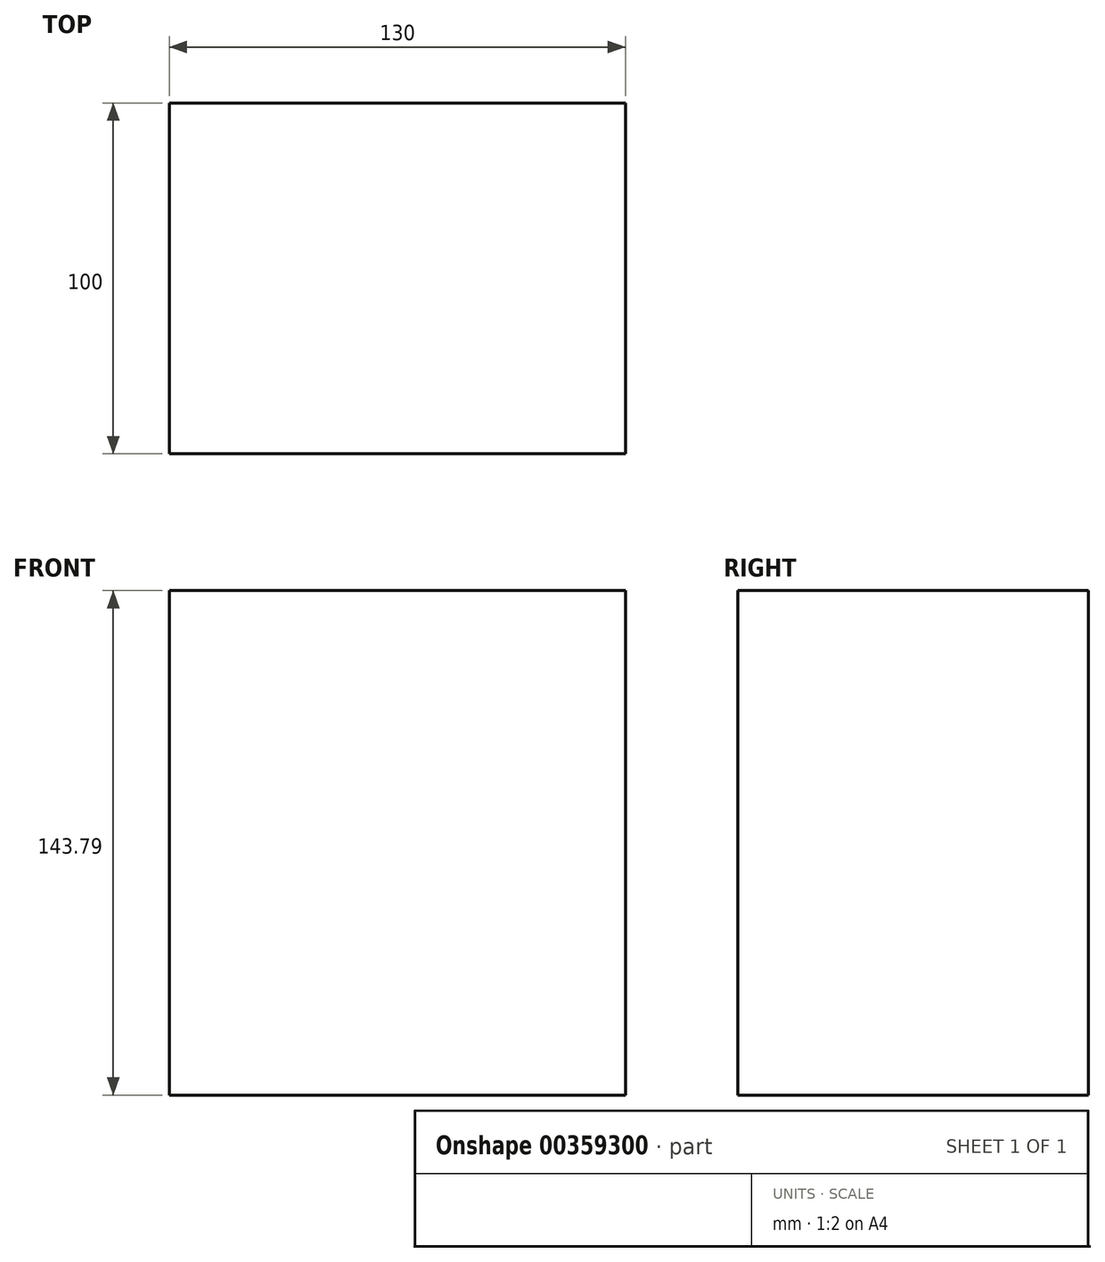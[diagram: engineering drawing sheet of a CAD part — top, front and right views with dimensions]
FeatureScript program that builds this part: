
annotation { "Feature Type Name" : "Feature", "Feature Type Description" : "" }
export const myFeature = defineFeature(function(context is Context, id is Id, definition is map)
    precondition{}
    {
        {
            var Q0;
            Q0=qCreatedBy(makeId("Top.planeOp"),FACE);
            var sketch = newSketch(context, id + "F0", { "sketchPlane" : qUnion([Q0])});
            skLineSegment(sketch, "E0.bottom", {"start": v(-65, 50) * mm, "end": v(65, 50) * mm});
            skLineSegment(sketch, "E0.top", {"start": v(-65, -50) * mm, "end": v(65, -50) * mm});
            skLineSegment(sketch, "E0.left", {"start": v(-65, 50) * mm, "end": v(-65, -50) * mm});
            skLineSegment(sketch, "E0.right", {"start": v(65, 50) * mm, "end": v(65, -50) * mm});
            skPoint(sketch, "E0.middle", {"position": v(0, 0) * mm});
            skSolve(sketch);
        }
        {
            var Q0;
            Q0=makeQuery(id+"F0.imprint","IMPRINT",FACE,{"disambiguationData":[TD([[makeQuery(id+"F0.imprint","IMPRINT",EDGE,{"derivedFrom":sQuery(id+"F0.wireOp",EDGE,"E0.bottom")}),-1.0]])]});
            extrude(context, id + "F1", {"entities" : qUnion([Q0]), "oppositeDirection" : true, "depth" : 180 * mm});
        }
        {
            var Q0;
            Q0=makeQuery(id+"F1.opExtrude","CAP_EDGE",EDGE,{"disambiguationData":[OSD([sQuery(id+"F0.wireOp",EDGE,"E0.right")])],"isStart":false});
            var Q1;
            Q1=makeQuery(id+"F1.opExtrude","CAP_EDGE",EDGE,{"disambiguationData":[OSD([sQuery(id+"F0.wireOp",EDGE,"E0.left")])],"isStart":false});
            fillet(context, id + "F2", {"entities" : qUnion([Q0, Q1]), "radius" : 36.2 * mm, "tangentPropagation" : true, "allowEdgeOverflow" : false});
        }
        {
            var Q0;
            Q0=makeQuery(id+"F1.opExtrude","SWEPT_FACE",FACE,{"disambiguationData":[OSD([sQuery(id+"F0.wireOp",EDGE,"E0.top")])]});
            var sketch = newSketch(context, id + "F3", { "sketchPlane" : qUnion([Q0])});
            skLineSegment(sketch, "E1", {"start": v(65, -143.79) * mm, "end": v(-65, -143.79) * mm});
            skSolve(sketch);
        }
        {
            var Q0;
            Q0 = qSketchRegion(id + "F3", true);
            var Q1;
            Q1=makeQuery(id+"F3.imprint","IMPRINT",FACE,{"disambiguationData":[TD([[makeQuery(id+"F3.imprint","IMPRINT",EDGE,{"derivedFrom":sQuery(id+"F3.wireOp",EDGE,"E1")}),1.0]])]});
            extrude(context, id + "F4", {"entities" : qUnion([Q0, Q1]), "operationType" : NewBodyOperationType.REMOVE, "oppositeDirection" : true, "depth" : 115 * mm});
        }
    });
